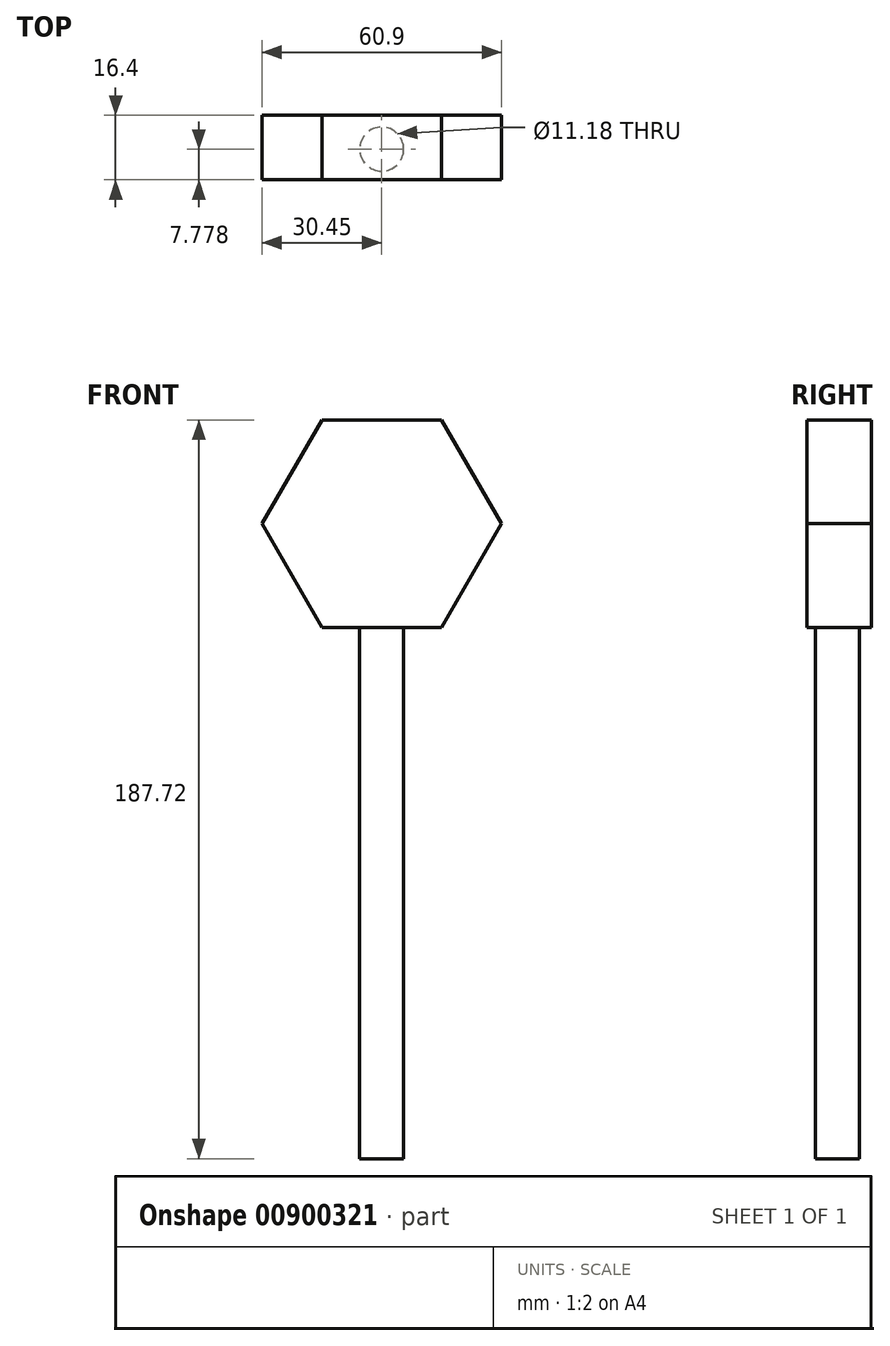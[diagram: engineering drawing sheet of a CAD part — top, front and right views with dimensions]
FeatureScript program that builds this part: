
annotation { "Feature Type Name" : "Feature", "Feature Type Description" : "" }
export const myFeature = defineFeature(function(context is Context, id is Id, definition is map)
    precondition{}
    {
        {
            var Q0;
            Q0=qCreatedBy(makeId("Front.planeOp"),FACE);
            var sketch = newSketch(context, id + "F0", { "sketchPlane" : qUnion([Q0])});
            skCircle(sketch, "E0.cCircle", {"center": v(0, 39.02) * mm, "radius": 26.37 * mm, "construction": true});
            skLineSegment(sketch, "E0.0", {"start": v(15.23, 12.65) * mm, "end": v(-15.23, 12.65) * mm});
            skLineSegment(sketch, "E0.1", {"start": v(-15.23, 12.65) * mm, "end": v(-30.45, 39.02) * mm});
            skLineSegment(sketch, "E0.2", {"start": v(-30.45, 39.02) * mm, "end": v(-15.23, 65.39) * mm});
            skLineSegment(sketch, "E0.3", {"start": v(-15.23, 65.39) * mm, "end": v(15.23, 65.39) * mm});
            skLineSegment(sketch, "E0.4", {"start": v(15.23, 65.39) * mm, "end": v(30.45, 39.02) * mm});
            skLineSegment(sketch, "E0.5", {"start": v(30.45, 39.02) * mm, "end": v(15.23, 12.65) * mm});
            skPoint(sketch, "E0.0.midPoint", {"position": v(0, 12.65) * mm});
            skSolve(sketch);
        }
        {
            var Q0;
            Q0=sQuery(id+"F0.wireOp",EDGE,"E0.1");
            var Q1;
            Q1=sQuery(id+"F0.wireOp",EDGE,"E0.2");
            var Q2;
            Q2=sQuery(id+"F0.wireOp",EDGE,"E0.3");
            var Q3;
            Q3=sQuery(id+"F0.wireOp",EDGE,"E0.4");
            var Q4;
            Q4=sQuery(id+"F0.wireOp",EDGE,"E0.0");
            var Q5;
            Q5=sQuery(id+"F0.wireOp",EDGE,"E0.5");
            extrude(context, id + "F1", {"bodyType" : ToolBodyType.SURFACE, "surfaceEntities" : qUnion([Q0, Q1, Q2, Q3, Q4, Q5]), "depth" : 16.4 * mm, "offsetDistance" : 25.4 * mm});
        }
        {
            var Q0;
            Q0=makeQuery(id+"F1.opExtrude","SWEPT_FACE",FACE,{"disambiguationData":[OSD([sQuery(id+"F0.wireOp",EDGE,"E0.0")])]});
            var sketch = newSketch(context, id + "F2", { "sketchPlane" : qUnion([Q0])});
            skCircle(sketch, "E1", {"center": v(0, -8.62) * mm, "radius": 5.59 * mm});
            skSolve(sketch);
        }
        {
            var Q0;
            Q0=sQuery(id+"F2.wireOp",EDGE,"E1");
            extrude(context, id + "F3", {"bodyType" : ToolBodyType.SURFACE, "surfaceEntities" : qUnion([Q0]), "oppositeDirection" : true, "depth" : 134.97 * mm, "offsetDistance" : 25.4 * mm});
        }
    });
